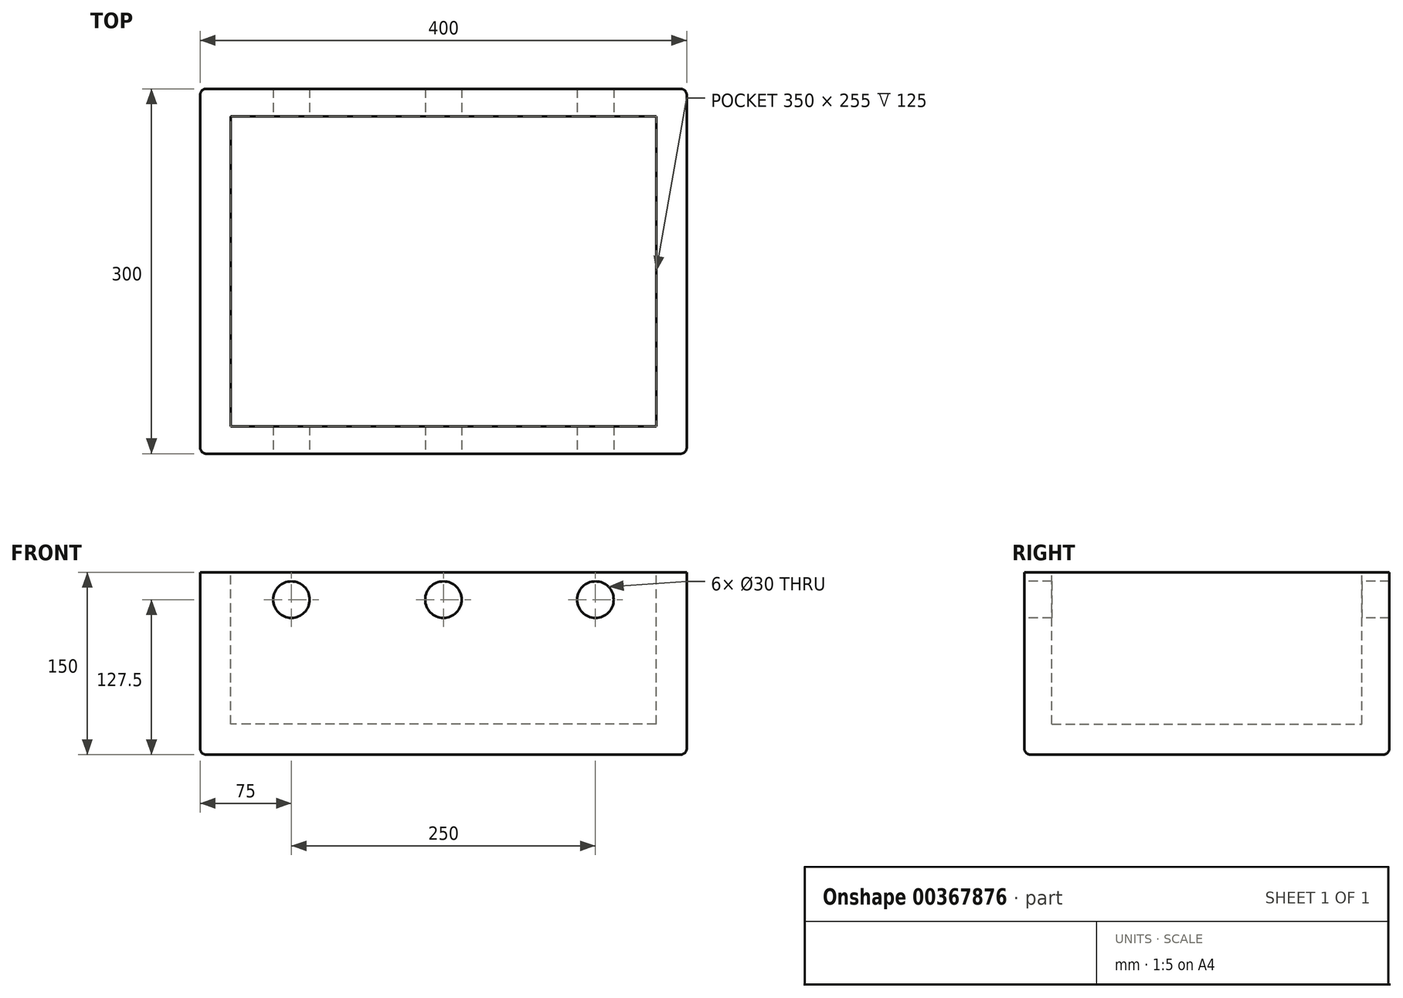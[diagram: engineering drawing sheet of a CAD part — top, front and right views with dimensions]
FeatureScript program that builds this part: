
annotation { "Feature Type Name" : "Feature", "Feature Type Description" : "" }
export const myFeature = defineFeature(function(context is Context, id is Id, definition is map)
    precondition{}
    {
        {
            var Q0;
            Q0=qCreatedBy(makeId("Top.planeOp"),FACE);
            var sketch = newSketch(context, id + "F0", { "sketchPlane" : qUnion([Q0])});
            skLineSegment(sketch, "E0.bottom", {"start": v(-200, 150) * mm, "end": v(200, 150) * mm});
            skLineSegment(sketch, "E0.top", {"start": v(-200, -150) * mm, "end": v(200, -150) * mm});
            skLineSegment(sketch, "E0.left", {"start": v(-200, 150) * mm, "end": v(-200, -150) * mm});
            skLineSegment(sketch, "E0.right", {"start": v(200, 150) * mm, "end": v(200, -150) * mm});
            skPoint(sketch, "E0.middle", {"position": v(0, 0) * mm});
            skSolve(sketch);
        }
        {
            var Q0;
            Q0 = qSketchRegion(id + "F0", true);
            extrude(context, id + "F1", {"entities" : qUnion([Q0]), "depth" : 150 * mm});
        }
        {
            var Q0;
            Q0=makeQuery(id+"F1.opExtrude","CAP_FACE",FACE,{"disambiguationData":[OSD([sQuery(id+"F0.wireOp",EDGE,"E0.bottom"),sQuery(id+"F0.wireOp",EDGE,"E0.top"),sQuery(id+"F0.wireOp",EDGE,"E0.left"),sQuery(id+"F0.wireOp",EDGE,"E0.right")])],"isStart":false});
            var sketch = newSketch(context, id + "F2", { "sketchPlane" : qUnion([Q0])});
            skLineSegment(sketch, "E1.bottom", {"start": v(175, -127.5) * mm, "end": v(-175, -127.5) * mm});
            skLineSegment(sketch, "E1.top", {"start": v(175, 127.5) * mm, "end": v(-175, 127.5) * mm});
            skLineSegment(sketch, "E1.left", {"start": v(175, -127.5) * mm, "end": v(175, 127.5) * mm});
            skLineSegment(sketch, "E1.right", {"start": v(-175, -127.5) * mm, "end": v(-175, 127.5) * mm});
            skPoint(sketch, "E1.middle", {"position": v(0, 0) * mm});
            skSolve(sketch);
        }
        {
            var Q0;
            Q0 = qSketchRegion(id + "F2", true);
            extrude(context, id + "F3", {"entities" : qUnion([Q0]), "operationType" : NewBodyOperationType.REMOVE, "oppositeDirection" : true, "depth" : 125 * mm});
        }
        {
            var Q0;
            Q0=makeQuery(id+"F1.opExtrude","SWEPT_EDGE",EDGE,{"disambiguationData":[OSD([sQuery(id+"F0.wireOp",EDGE,"E0.bottom"),sQuery(id+"F0.wireOp",EDGE,"E0.right")])]});
            var Q1;
            Q1=makeQuery(id+"F1.opExtrude","SWEPT_EDGE",EDGE,{"disambiguationData":[OSD([sQuery(id+"F0.wireOp",EDGE,"E0.top"),sQuery(id+"F0.wireOp",EDGE,"E0.right")])]});
            var Q2;
            Q2=makeQuery(id+"F1.opExtrude","SWEPT_EDGE",EDGE,{"disambiguationData":[OSD([sQuery(id+"F0.wireOp",EDGE,"E0.top"),sQuery(id+"F0.wireOp",EDGE,"E0.left")])]});
            var Q3;
            Q3=makeQuery(id+"F1.opExtrude","CAP_EDGE",EDGE,{"disambiguationData":[OSD([sQuery(id+"F0.wireOp",EDGE,"E0.left")])],"isStart":true});
            var Q4;
            Q4=makeQuery(id+"F1.opExtrude","CAP_EDGE",EDGE,{"disambiguationData":[OSD([sQuery(id+"F0.wireOp",EDGE,"E0.top")])],"isStart":true});
            var Q5;
            Q5=makeQuery(id+"F1.opExtrude","CAP_EDGE",EDGE,{"disambiguationData":[OSD([sQuery(id+"F0.wireOp",EDGE,"E0.right")])],"isStart":true});
            var Q6;
            Q6=makeQuery(id+"F1.opExtrude","CAP_EDGE",EDGE,{"disambiguationData":[OSD([sQuery(id+"F0.wireOp",EDGE,"E0.bottom")])],"isStart":true});
            var Q7;
            Q7=makeQuery(id+"F1.opExtrude","SWEPT_EDGE",EDGE,{"disambiguationData":[OSD([sQuery(id+"F0.wireOp",EDGE,"E0.bottom"),sQuery(id+"F0.wireOp",EDGE,"E0.left")])]});
            fillet(context, id + "F4", {"entities" : qUnion([Q0, Q1, Q2, Q3, Q4, Q5, Q6, Q7]), "radius" : 5 * mm, "tangentPropagation" : true, "allowEdgeOverflow" : false});
        }
        {
            var Q0;
            Q0=makeQuery(id+"F3.boolean.opBoolean","COPY",FACE,{"derivedFrom":makeQuery(id+"F3.opExtrude","SWEPT_FACE",FACE,{"disambiguationData":[OSD([sQuery(id+"F2.wireOp",EDGE,"E1.bottom")])]})});
            var sketch = newSketch(context, id + "F5", { "sketchPlane" : qUnion([Q0])});
            skCircle(sketch, "E2", {"center": v(125, 127.5) * mm, "radius": 15 * mm});
            skCircle(sketch, "E3", {"center": v(-125, 127.5) * mm, "radius": 15 * mm});
            skCircle(sketch, "E4", {"center": v(0, 127.5) * mm, "radius": 15 * mm});
            skSolve(sketch);
        }
        {
            var Q0;
            Q0 = qSketchRegion(id + "F5", true);
            extrude(context, id + "F6", {"entities" : qUnion([Q0]), "operationType" : NewBodyOperationType.REMOVE, "endBound" : BoundingType.SYMMETRIC, "depth" : 804 * mm});
        }
    });
